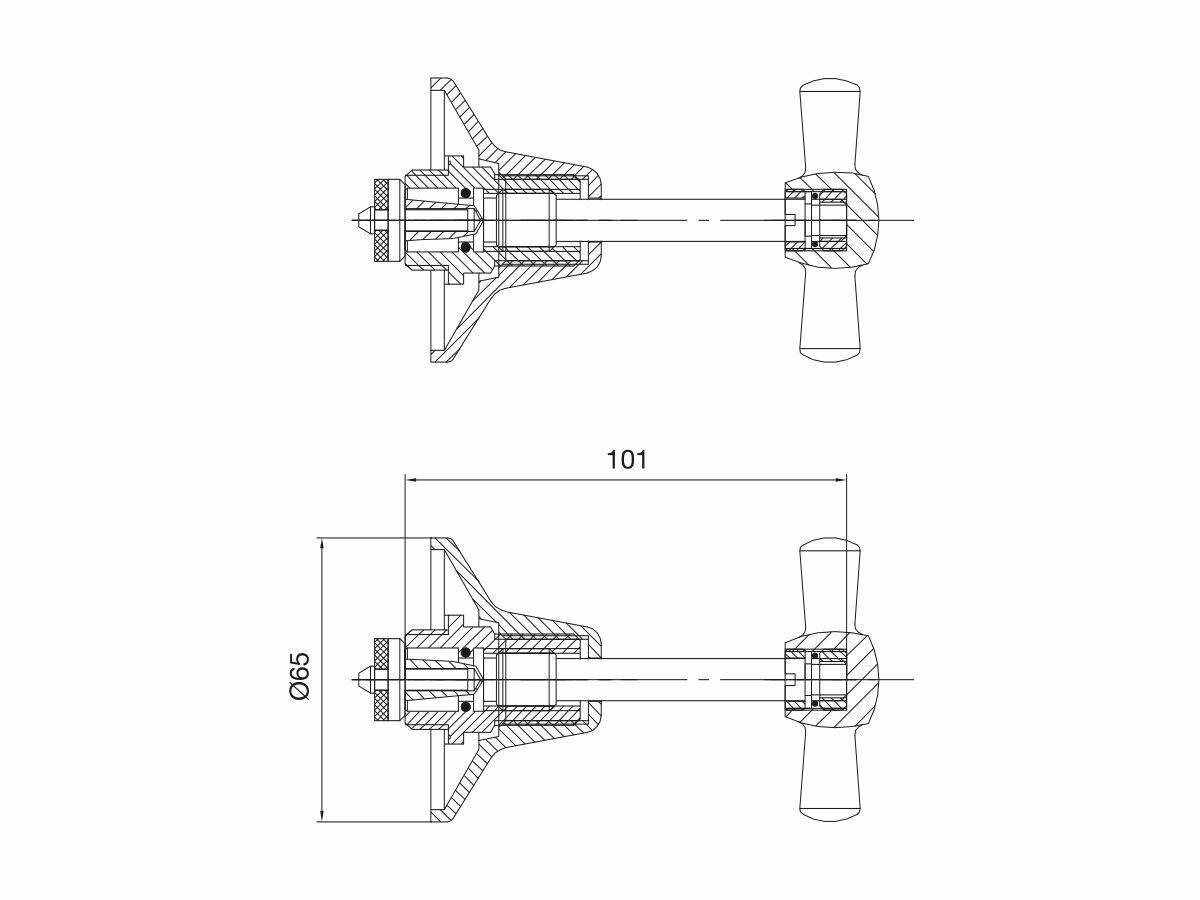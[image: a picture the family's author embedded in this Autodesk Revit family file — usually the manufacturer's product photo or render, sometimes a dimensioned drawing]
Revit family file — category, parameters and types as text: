
# Revit family: Reece_Tap_Base_Wall Sink Set_Anti-Vandal
name_source: partatom
category: Plumbing Fixtures
revit_build: Autodesk Revit 2018 (Build: 20190510_1515(x64)
units: mm (PartAtom-declared; Revit-internal decimal feet)

## family parameters
Cut with Voids When Loaded = No
Host = Face
Part Type = Normal
Room Calculation Point = Yes
Round Connector Dimension = Use Diameter
Shared = Yes

## types (1)
- 224.3 mm_Chrome
    CWFU = 0
    Default Elevation = 1000 mm  [stored 3.28084 ft]
    Description = Base Wall Sink Set Anti-Vandal Chrome (4 Star)
    Disclaimer = THIS FILE IS THE PROPERTY OF THE REECE GROUP. IT MAY NOT BE REPRODUCED, REVERSE-ENGINEERED OR MODIFIED. ANY REPUBLICATION, TRANSMISSION OR DISTRIBUTION FOR THE PURPOSE OF COMMERCIALLY EXPLOITING THE FILES IS PROHIBITED.
    HWFU = 0
    Keynote = Product #9505434, Reece_Tap_Base_Wall Sink Set_Anti-Vandal - 224.3 mm_Chrome
    Manufacturer = Base
    Model = Base
    Reece_Detail_Additional = Anti-Vandal
    Reece_Detail_Disclaimer = THIS FILE IS THE PROPERTY OF THE REECE GROUP. IT MAY NOT BE REPRODUCED, REVERSE-ENGINEERED OR MODIFIED. ANY REPUBLICATION, TRANSMISSION OR DISTRIBUTION FOR THE PURPOSE OF COMMERCIALLY EXPLOITING THE FILES IS PROHIBITED.
    Reece_Material-Main = Reece_Brass_Chrome
    Reece_Overall_Diameter = 65 mm  [stored 0.213255 ft]
    Reece_Product_Brand = Base
    Reece_Product_Description = Base Wall Sink Set Anti-Vandal Chrome (4 Star)
    Reece_Product_Mount = Wall Mounted
    Reece_Product_Number = 9505434
    Reece_Product_Sub Brand = Base
    Reece_Product_Type = Tap
    Reece_Product_Web Page = https://www.reece.com.au
    Reece_Tap_Inlet = 12 mm  [stored 0.0393701 ft]
    Reece_Tap_Reach = 224 mm
    Type Comments = Tap
    URL = https://www.reece.com.au
    WFU = 0

note: [stored X ft] marks values corroborated as IEEE doubles in the binary element streams (Revit-internal decimal feet)

## geometry (parser evidence)
native form markers: Sweep x5
no freeform markers — native parametric forms only
